# Revit family: FU_Table_Sandler_Plania_PL30110
name_source: partatom
category: Furniture
units: mm (PartAtom-declared; Revit-internal decimal feet)

## family parameters
Always vertical = Yes
Cut with Voids When Loaded = No
OmniClass Number = 23.40.20.00
OmniClass Title = General Furniture and Specialties
Room Calculation Point = No
Shared = No
Work Plane-Based = No

## types (1)
- PL30110
    Default Elevation = 0 mm  [stored 0 ft]
    Depth = 695 mm  [stored 2.28018 ft]
    Description = Set of ML01 table legs for Plania tables with a height of 29.5″ for tables 36″ wide. Please note 2 sets of legs are required for each table / bench, assembly required
    Height = 691 mm
    Manufacturer = Sandler
    Model = Plania PL30110
    URL = https://www.sandlerseating.com
    Width = 145 mm
    Wood Finish = Wood - Oak - Natural - V

note: [stored X ft] marks values corroborated as IEEE doubles in the binary element streams (Revit-internal decimal feet)

## geometry (parser evidence)
native form markers: Sweep x3
no freeform markers — native parametric forms only
